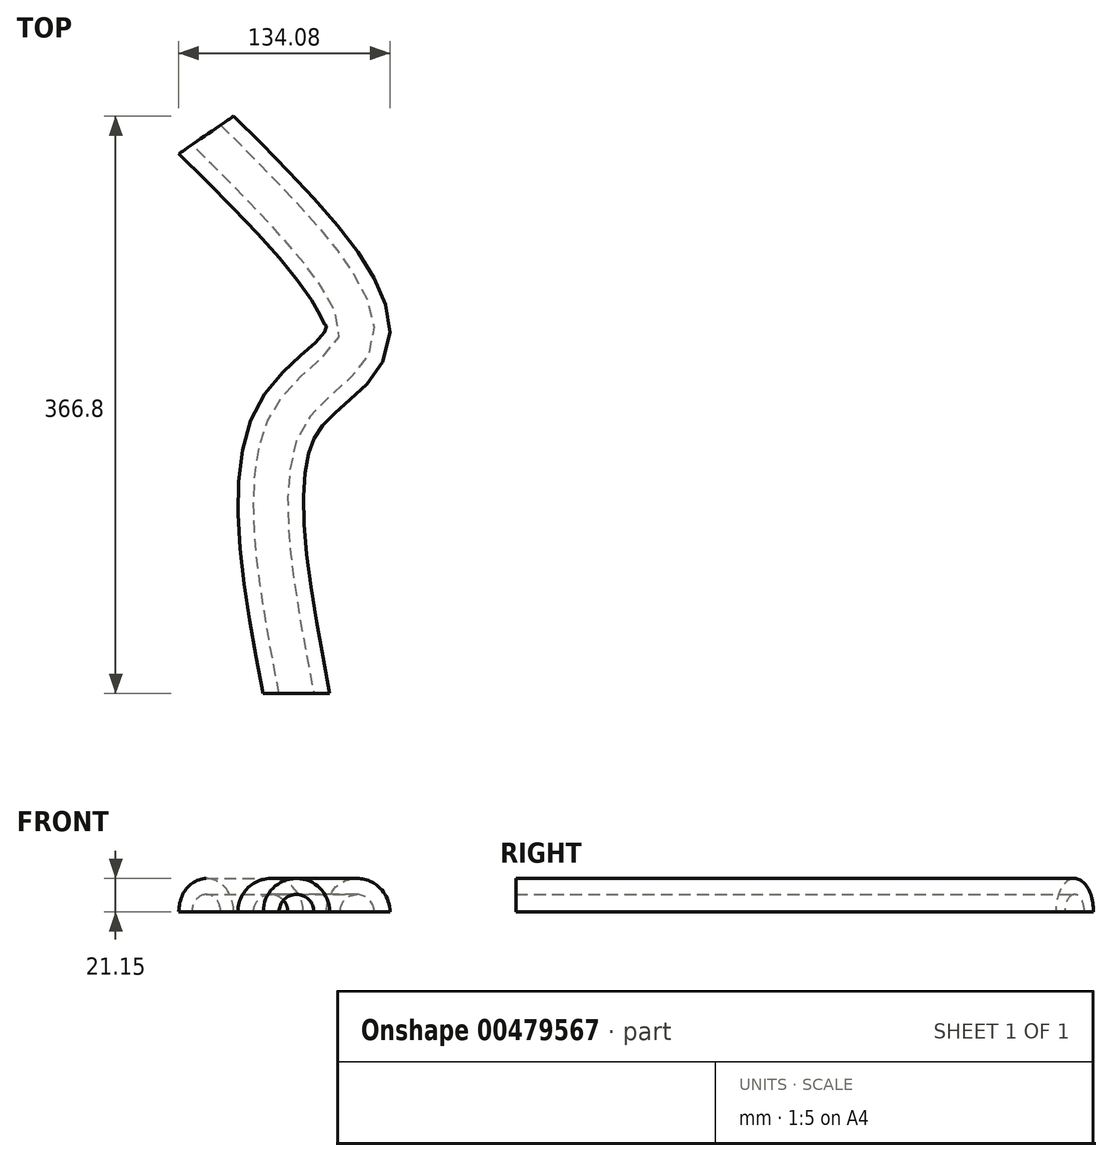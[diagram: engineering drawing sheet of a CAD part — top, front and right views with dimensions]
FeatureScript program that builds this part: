
annotation { "Feature Type Name" : "Feature", "Feature Type Description" : "" }
export const myFeature = defineFeature(function(context is Context, id is Id, definition is map)
    precondition{}
    {
        {
            var Q0;
            Q0=qCreatedBy(makeId("Top.planeOp"),FACE);
            var sketch = newSketch(context, id + "F0", { "sketchPlane" : qUnion([Q0])});
            skFitSpline(sketch, "E0", {"points": [v(-106.66, 105.3) * mm, v(-11.3, -23.46) * mm, v(-54.37, -74.43) * mm, v(-49.34, -249.7) * mm], "startDerivative": vector(405.98, -403.19) * mm, "endDerivative": vector(102.25, -535.93) * mm});
            skSolve(sketch);
        }
        {
            var Q0;
            Q0=qCreatedBy(makeId("Front.planeOp"),FACE);
            var Q1;
            Q1=sQuery(id+"F0.wireOp",VERTEX,"E0.end");
            cPlane(context, id + "F1", {"entities" : qUnion([Q0, Q1]), "cplaneType" : CPlaneType.PLANE_POINT, "offset" : 150 * mm, "width" : 150 * mm, "height" : 150 * mm});
        }
        {
            var Q0;
            Q0=qCreatedBy(id+"F1.planeOp",FACE);
            var sketch = newSketch(context, id + "F2", { "sketchPlane" : qUnion([Q0])});
            skLineSegment(sketch, "E1", {"start": v(-131.65, 0) * mm, "end": v(39.09, 0) * mm, "construction": true});
            skArc(sketch, "E2", {"start": v(-28.45, 0) * mm, "mid": v(-49.6, 21.15) * mm, "end": v(-70.76, 0) * mm});
            skLineSegment(sketch, "E3", {"start": v(-70.76, 0) * mm, "end": v(-28.45, 0) * mm});
            skSolve(sketch);
        }
        {
            var Q0;
            Q0=makeQuery(id+"F2.imprint","IMPRINT",FACE,{"disambiguationData":[TD([[makeQuery(id+"F2.imprint","IMPRINT",EDGE,{"derivedFrom":sQuery(id+"F2.wireOp",EDGE,"E2")}),1.0]])]});
            var Q1;
            Q1=sQuery(id+"F0.wireOp",EDGE,"E0");
            sweep(context, id + "F3", {"profiles" : qUnion([Q0]), "path" : qUnion([Q1])});
        }
        {
            var Q0;
            Q0=qCreatedBy(id+"F1.planeOp",FACE);
            var sketch = newSketch(context, id + "F4", { "sketchPlane" : qUnion([Q0])});
            skCircle(sketch, "E4", {"center": v(-49.6, 0) * mm, "radius": 11.02 * mm});
            skSolve(sketch);
        }
        {
            var Q0;
            Q0=qSketchRegion(id+"F4",true);
            var Q1;
            Q1=sQuery(id+"F0.wireOp",EDGE,"E0");
            sweep(context, id + "F5", {"operationType" : NewBodyOperationType.REMOVE, "profiles" : qUnion([Q0]), "path" : qUnion([Q1])});
        }
    });
